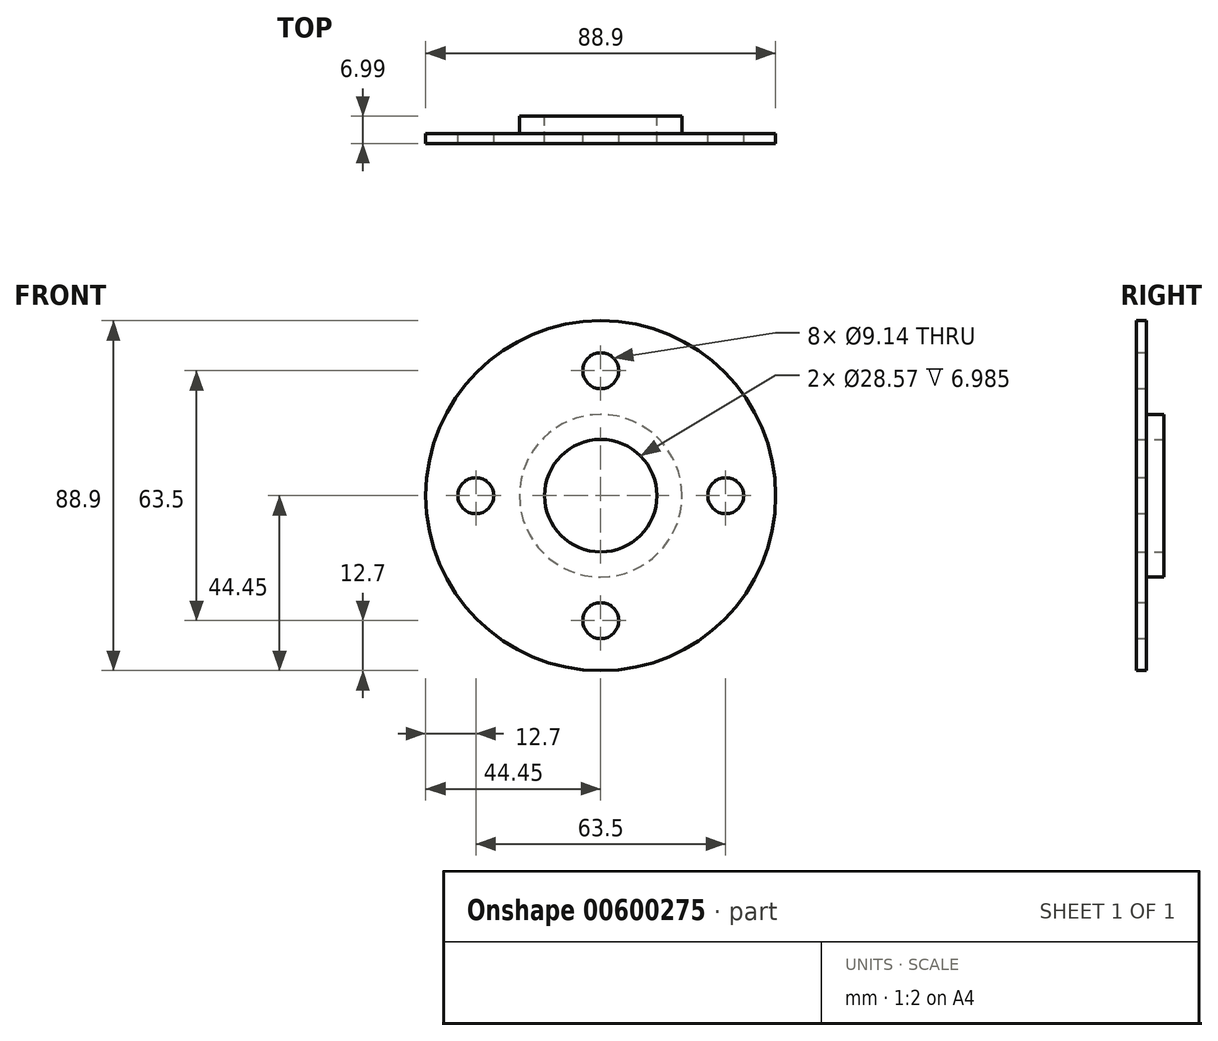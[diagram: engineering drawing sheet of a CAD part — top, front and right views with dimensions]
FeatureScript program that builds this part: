
annotation { "Feature Type Name" : "Feature", "Feature Type Description" : "" }
export const myFeature = defineFeature(function(context is Context, id is Id, definition is map)
    precondition{}
    {
        {
            var Q0;
            Q0=qCreatedBy(makeId("Right.planeOp"),FACE);
            var sketch = newSketch(context, id + "F0", { "sketchPlane" : qUnion([Q0])});
            skLineSegment(sketch, "E0", {"start": v(0, 0) * mm, "end": v(0, 44.45) * mm});
            skLineSegment(sketch, "E1", {"start": v(0, 44.45) * mm, "end": v(2.54, 44.45) * mm});
            skLineSegment(sketch, "E2", {"start": v(2.54, 44.45) * mm, "end": v(2.54, 20.64) * mm});
            skLineSegment(sketch, "E3", {"start": v(2.54, 20.64) * mm, "end": v(6.99, 20.64) * mm});
            skLineSegment(sketch, "E4", {"start": v(6.99, 20.64) * mm, "end": v(6.99, 0) * mm});
            skLineSegment(sketch, "E5", {"start": v(6.99, 0) * mm, "end": v(0, 0) * mm});
            skLineSegment(sketch, "E6", {"start": v(0, 0) * mm, "end": v(12.7, 0) * mm});
            skSolve(sketch);
        }
        {
            var Q0;
            {var subQ0=sQuery(id+"F0.wireOp",EDGE,"E0");Q0=makeQuery(id+"F0.imprint","IMPRINT",FACE,{"disambiguationData":[TD([[makeQuery(id+"F0.imprint","IMPRINT",EDGE,{"derivedFrom":subQ0}),-1.0]])]});}
            var Q1;
            Q1=sQuery(id+"F0.wireOp",EDGE,"E6");
            revolve(context, id + "F1", {"entities" : qUnion([Q0]), "axis" : qUnion([Q1]), "revolveType" : RevolveType.FULL});
        }
        {
            var Q0;
            Q0=qCreatedBy(makeId("Front.planeOp"),FACE);
            var sketch = newSketch(context, id + "F2", { "sketchPlane" : qUnion([Q0])});
            skCircle(sketch, "E7", {"center": v(0, 0) * mm, "radius": 31.75 * mm});
            skCircle(sketch, "E8", {"center": v(0, 31.75) * mm, "radius": 4.57 * mm});
            skCircle(sketch, "E9.1.0", {"center": v(-31.75, 0) * mm, "radius": 4.57 * mm});
            skCircle(sketch, "E9.2.0", {"center": v(0, -31.75) * mm, "radius": 4.57 * mm});
            skCircle(sketch, "E9.3.0", {"center": v(31.75, 0) * mm, "radius": 4.57 * mm});
            skSolve(sketch);
        }
        {
            var Q0;
            Q0=sQuery(id+"F2.wireOp",VERTEX,"E7.center");
            var Q1;
            Q1=makeQuery(id+"F1.opRevolve","SWEPT_BODY",BODY,{"disambiguationData":[OSD([sQuery(id+"F0.wireOp",EDGE,"E0"),sQuery(id+"F0.wireOp",EDGE,"E1"),sQuery(id+"F0.wireOp",EDGE,"E2"),sQuery(id+"F0.wireOp",EDGE,"E3"),sQuery(id+"F0.wireOp",EDGE,"E4"),sQuery(id+"F0.wireOp",EDGE,"E6")])]});
            hole(context, id + "F3", {"style" : HoleStyle.SIMPLE, "endStyle" : HoleEndStyle.THROUGH, "holeDiameter" : 28.57 * mm, "majorDiameter" : 6.35 * mm, "isTappedThrough" : true, "tappedDepth" : 12.7 * mm, "tapClearance" : 3, "startFromSketch" : true, "locations" : qUnion([Q0]), "scope" : qUnion([Q1])});
        }
        {
            var Q0;
            Q0=sQuery(id+"F2.wireOp",VERTEX,"E8.center");
            var Q1;
            Q1=sQuery(id+"F2.wireOp",VERTEX,"E9.3.0.center");
            var Q2;
            Q2=sQuery(id+"F2.wireOp",VERTEX,"E9.2.0.center");
            var Q3;
            Q3=sQuery(id+"F2.wireOp",VERTEX,"E9.1.0.center");
            var Q4;
            Q4=makeQuery(id+"F1.opRevolve","SWEPT_BODY",BODY,{"disambiguationData":[OSD([sQuery(id+"F0.wireOp",EDGE,"E0"),sQuery(id+"F0.wireOp",EDGE,"E1"),sQuery(id+"F0.wireOp",EDGE,"E2"),sQuery(id+"F0.wireOp",EDGE,"E3"),sQuery(id+"F0.wireOp",EDGE,"E4"),sQuery(id+"F0.wireOp",EDGE,"E6")])]});
            hole(context, id + "F4", {"style" : HoleStyle.SIMPLE, "endStyle" : HoleEndStyle.THROUGH, "holeDiameter" : 9.14 * mm, "majorDiameter" : 6.35 * mm, "isTappedThrough" : true, "tappedDepth" : 12.7 * mm, "tapClearance" : 3, "startFromSketch" : true, "locations" : qUnion([Q0, Q1, Q2, Q3]), "scope" : qUnion([Q4])});
        }
    });
